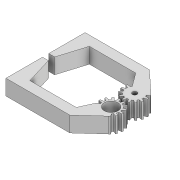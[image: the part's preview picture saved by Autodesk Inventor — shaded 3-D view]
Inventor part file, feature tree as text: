
AUTODESK INVENTOR PART (.ipt)
format: ipt  version: 2021 (Build 250183000, 183)  size: 234,496 bytes
history: native  units: mm
features: other x1, extrude x1, sketch x1
ambient origin geometry x8: Origin, YZ Plane, XZ Plane, XY Plane, X Axis, Y Axis, Z Axis, Center Point
bodies: Body1 (feature_tree)
feature tree (3):
  other  "Sólido1"
  extrude  "Extrusión1"  Depth=10.0mm
  sketch  "Boceto1"  dims[d1=9.0mm d2=11.0mm d3=15.0mm d9=140.0mm d11=360.0deg d16=20.0mm d19=30.0mm d21=140.0mm d30=6.3mm d31=3.0mm d32=10.0mm d33=0.0mm]
